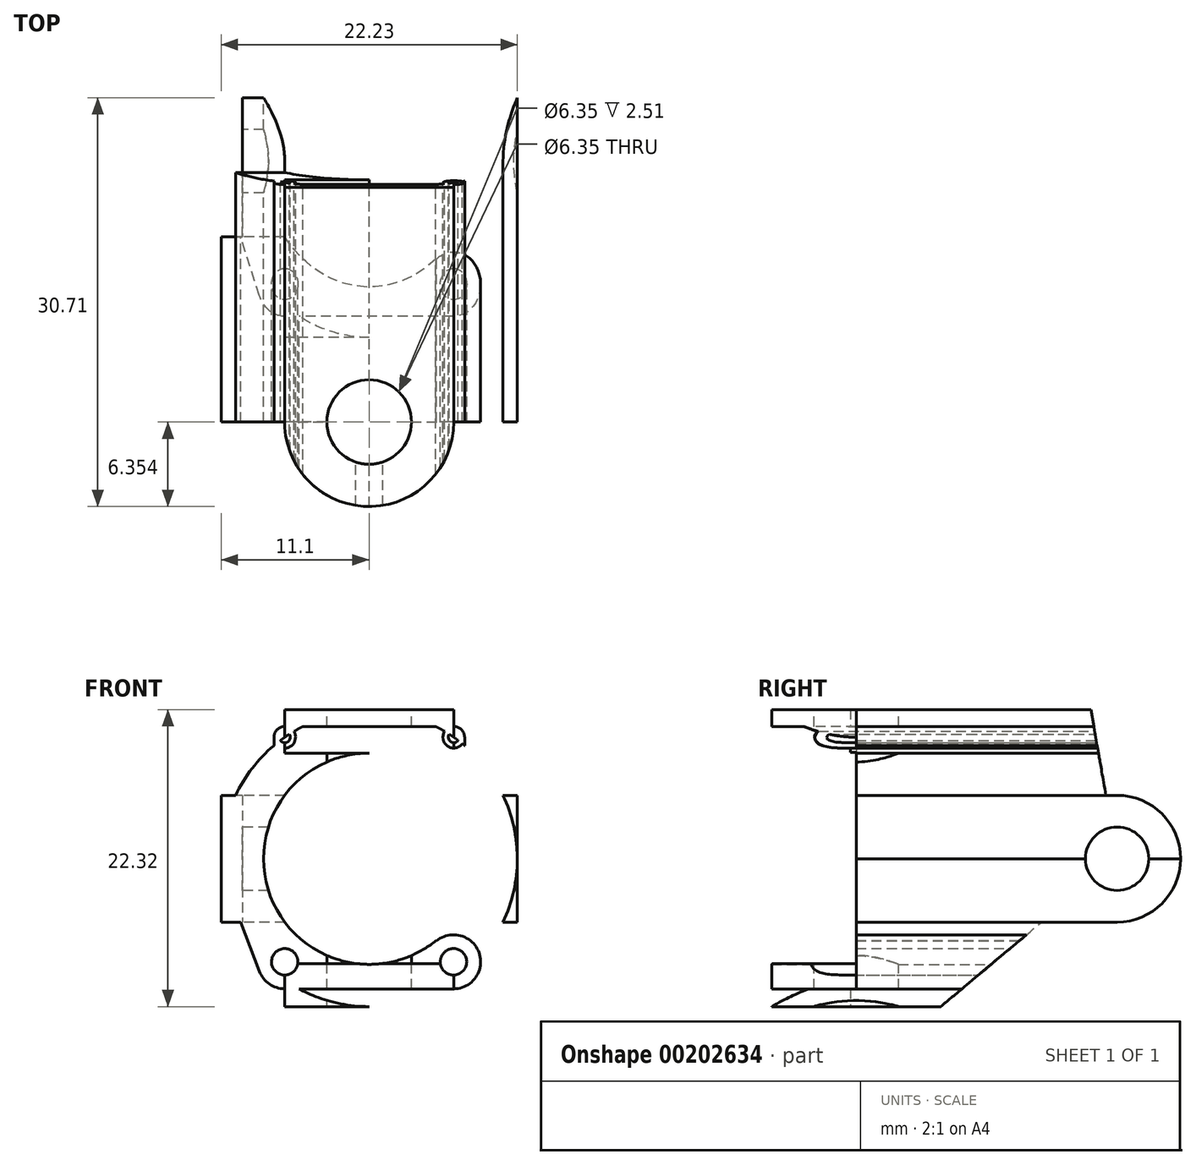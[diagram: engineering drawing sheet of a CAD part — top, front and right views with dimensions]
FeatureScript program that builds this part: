
annotation { "Feature Type Name" : "Feature", "Feature Type Description" : "" }
export const myFeature = defineFeature(function(context is Context, id is Id, definition is map)
    precondition{}
    {
        {
            var Q0;
            Q0=qCreatedBy(makeId("Front.planeOp"),FACE);
            var sketch = newSketch(context, id + "F0", { "sketchPlane" : qUnion([Q0])});
            skCircle(sketch, "E0", {"center": v(0, -0.64) * mm, "radius": 7.94 * mm});
            skCircle(sketch, "E1", {"center": v(0, -0.64) * mm, "radius": 9.53 * mm});
            skCircle(sketch, "E2", {"center": v(0, -0.64) * mm, "radius": 11.11 * mm});
            skLineSegment(sketch, "E3", {"start": v(-12.13, -0.64) * mm, "end": v(12.7, -0.64) * mm});
            skLineSegment(sketch, "E4", {"start": v(0, 12.07) * mm, "end": v(0, -13.22) * mm, "construction": true});
            skArc(sketch, "E5", {"start": v(-11.12, -0.64) * mm, "mid": v(-7.45, -7.6) * mm, "end": v(0, -10.16) * mm});
            skArc(sketch, "E6", {"start": v(0, -10.16) * mm, "mid": v(7.44, -7.6) * mm, "end": v(11.1, -0.64) * mm});
            skLineSegment(sketch, "E7", {"start": v(-9.92, -10.16) * mm, "end": v(10.05, -10.18) * mm, "construction": true});
            skLineSegment(sketch, "E8", {"start": v(-9.95, -8.38) * mm, "end": v(9.97, -8.38) * mm});
            skLineSegment(sketch, "E9", {"start": v(-6.36, -11.59) * mm, "end": v(-6.36, 12.24) * mm});
            skLineSegment(sketch, "E10", {"start": v(6.32, -11.83) * mm, "end": v(6.34, 12.33) * mm});
            skCircle(sketch, "E11", {"center": v(6.32, -8.38) * mm, "radius": 1 * mm});
            skCircle(sketch, "E12", {"center": v(6.32, -8.38) * mm, "radius": 2.03 * mm});
            skCircle(sketch, "E13", {"center": v(-6.36, -8.38) * mm, "radius": 1 * mm});
            skCircle(sketch, "E14", {"center": v(-6.36, -8.38) * mm, "radius": 2.03 * mm});
            skLineSegment(sketch, "E15", {"start": v(-10.46, -3.36) * mm, "end": v(-8.25, -9.11) * mm});
            skLineSegment(sketch, "E16", {"start": v(10.4, -3.48) * mm, "end": v(8.22, -9.12) * mm});
            skLineSegment(sketch, "E17", {"start": v(-6.36, -10.41) * mm, "end": v(6.32, -10.41) * mm});
            skCircle(sketch, "E18", {"center": v(6.34, 8.49) * mm, "radius": 0.4 * mm});
            skCircle(sketch, "E19", {"center": v(-6.36, 8.48) * mm, "radius": 0.4 * mm});
            skCircle(sketch, "E20", {"center": v(-6.36, 8.48) * mm, "radius": 0.81 * mm});
            skCircle(sketch, "E21", {"center": v(6.34, 8.49) * mm, "radius": 0.81 * mm});
            skLineSegment(sketch, "E22", {"start": v(-6.36, 9.3) * mm, "end": v(-2.52, 10.19) * mm});
            skLineSegment(sketch, "E23", {"start": v(6.34, 9.3) * mm, "end": v(2.5, 10.19) * mm});
            skLineSegment(sketch, "E24", {"start": v(5.84, 8.49) * mm, "end": v(7.39, 8.49) * mm, "construction": true});
            skLineSegment(sketch, "E25", {"start": v(-5.8, 8.48) * mm, "end": v(-7.52, 8.48) * mm, "construction": true});
            skLineSegment(sketch, "E26", {"start": v(-7.17, 8.48) * mm, "end": v(-7.17, 7.86) * mm});
            skLineSegment(sketch, "E27", {"start": v(7.15, 8.49) * mm, "end": v(7.15, 7.86) * mm});
            skLineSegment(sketch, "E28", {"start": v(7.93, -0.64) * mm, "end": v(7.93, 10.72) * mm, "construction": true});
            skLineSegment(sketch, "E29", {"start": v(-7.94, -0.64) * mm, "end": v(-7.94, 9.8) * mm, "construction": true});
            skLineSegment(sketch, "E30.bottom", {"start": v(7.93, 4.13) * mm, "end": v(11.1, 4.13) * mm});
            skLineSegment(sketch, "E30.top", {"start": v(7.93, -5.4) * mm, "end": v(11.1, -5.4) * mm});
            skLineSegment(sketch, "E30.left", {"start": v(7.93, 4.13) * mm, "end": v(7.93, -5.4) * mm});
            skLineSegment(sketch, "E30.right", {"start": v(11.1, 4.13) * mm, "end": v(11.1, -5.4) * mm});
            skLineSegment(sketch, "E31.bottom", {"start": v(-7.94, 4.13) * mm, "end": v(-11.12, 4.13) * mm});
            skLineSegment(sketch, "E31.top", {"start": v(-7.94, -5.4) * mm, "end": v(-11.12, -5.4) * mm});
            skLineSegment(sketch, "E31.left", {"start": v(-7.94, 4.13) * mm, "end": v(-7.94, -5.4) * mm});
            skLineSegment(sketch, "E31.right", {"start": v(-11.12, 4.13) * mm, "end": v(-11.12, -5.4) * mm});
            skLineSegment(sketch, "E32", {"start": v(-7.94, -5.4) * mm, "end": v(7.93, -5.4) * mm});
            skLineSegment(sketch, "E33.bottom", {"start": v(6.34, 9.3) * mm, "end": v(-6.36, 9.3) * mm});
            skLineSegment(sketch, "E33.top", {"start": v(6.34, 10.57) * mm, "end": v(-6.36, 10.57) * mm});
            skLineSegment(sketch, "E33.left", {"start": v(6.34, 9.3) * mm, "end": v(6.34, 10.57) * mm});
            skLineSegment(sketch, "E33.right", {"start": v(-6.36, 9.3) * mm, "end": v(-6.36, 10.57) * mm});
            skLineSegment(sketch, "E34", {"start": v(0, 7.3) * mm, "end": v(11, 7.3) * mm});
            skLineSegment(sketch, "E35", {"start": v(11, 7.3) * mm, "end": v(-10.84, 7.3) * mm});
            skLineSegment(sketch, "E36.bottom", {"start": v(6.32, -10.41) * mm, "end": v(0, -10.41) * mm});
            skLineSegment(sketch, "E36.top", {"start": v(6.32, -11.75) * mm, "end": v(0, -11.75) * mm});
            skLineSegment(sketch, "E36.left", {"start": v(6.32, -10.41) * mm, "end": v(6.32, -11.75) * mm});
            skLineSegment(sketch, "E36.right", {"start": v(0, -10.41) * mm, "end": v(0, -11.75) * mm});
            skLineSegment(sketch, "E37.bottom", {"start": v(-6.36, -10.41) * mm, "end": v(0, -10.41) * mm});
            skLineSegment(sketch, "E37.top", {"start": v(-6.36, -11.75) * mm, "end": v(0, -11.75) * mm});
            skLineSegment(sketch, "E37.left", {"start": v(-6.36, -10.41) * mm, "end": v(-6.36, -11.75) * mm});
            skLineSegment(sketch, "E38", {"start": v(6.32, -8.38) * mm, "end": v(0, -0.64) * mm});
            skSolve(sketch);
        }
        {
            var Q0;
            {var subQ0=sQuery(id+"F0.wireOp",EDGE,"E35");var subQ15=sQuery(id+"F0.wireOp",EDGE,"E1");var subQ16=makeQuery(id+"F0.imprint","INTERSECT",VERTEX,{"disambiguationData":[OD(0.0)],"derivedFrom":[subQ15,subQ0]});Q0=makeQuery(id+"F0.imprint","IMPRINT",FACE,{"disambiguationData":[TD([[makeQuery(id+"F0.imprint","IMPRINT",EDGE,{"disambiguationData":[TD([[subQ16,-1.0]])],"derivedFrom":subQ15}),-1.0]])]});}
            var Q1;
            {var subQ0=sQuery(id+"F0.wireOp",EDGE,"E35");var subQ1=sQuery(id+"F0.wireOp",EDGE,"E1");var subQ2=makeQuery(id+"F0.imprint","INTERSECT",VERTEX,{"disambiguationData":[OD(0.0)],"derivedFrom":[subQ1,subQ0]});Q1=makeQuery(id+"F0.imprint","IMPRINT",FACE,{"disambiguationData":[TD([[makeQuery(id+"F0.imprint","IMPRINT",EDGE,{"disambiguationData":[TD([[subQ2,-1.0]])],"derivedFrom":subQ1}),1.0]])]});}
            var Q2;
            {var subQ0=sQuery(id+"F0.wireOp",EDGE,"E18");var subQ1=sQuery(id+"F0.wireOp",EDGE,"E2");var subQ2=makeQuery(id+"F0.imprint","INTERSECT",VERTEX,{"disambiguationData":[OD(1.0)],"derivedFrom":[subQ1,subQ0]});Q2=makeQuery(id+"F0.imprint","IMPRINT",FACE,{"disambiguationData":[TD([[makeQuery(id+"F0.imprint","IMPRINT",EDGE,{"disambiguationData":[TD([[subQ2,-1.0]])],"derivedFrom":subQ1}),1.0]])]});}
            var Q3;
            {var subQ0=sQuery(id+"F0.wireOp",EDGE,"E21");var subQ1=sQuery(id+"F0.wireOp",EDGE,"E2");var subQ2=makeQuery(id+"F0.imprint","INTERSECT",VERTEX,{"disambiguationData":[OD(0.0)],"derivedFrom":[subQ1,subQ0]});Q3=makeQuery(id+"F0.imprint","IMPRINT",FACE,{"disambiguationData":[TD([[makeQuery(id+"F0.imprint","IMPRINT",EDGE,{"disambiguationData":[TD([[subQ2,-1.0]])],"derivedFrom":subQ1}),1.0]])]});}
            var Q4;
            {var subQ1=sQuery(id+"F0.wireOp",EDGE,"E2");var subQ5=sQuery(id+"F0.wireOp",EDGE,"E21");var subQ8=makeQuery(id+"F0.imprint","INTERSECT",VERTEX,{"disambiguationData":[OD(0.0)],"derivedFrom":[subQ1,subQ5]});Q4=makeQuery(id+"F0.imprint","IMPRINT",FACE,{"disambiguationData":[TD([[makeQuery(id+"F0.imprint","IMPRINT",EDGE,{"disambiguationData":[TD([[subQ8,-1.0]])],"derivedFrom":subQ1}),-1.0]])]});}
            var Q5;
            {var subQ0=sQuery(id+"F0.wireOp",EDGE,"E18");var subQ1=sQuery(id+"F0.wireOp",EDGE,"E2");var subQ2=makeQuery(id+"F0.imprint","INTERSECT",VERTEX,{"disambiguationData":[OD(1.0)],"derivedFrom":[subQ1,subQ0]});Q5=makeQuery(id+"F0.imprint","IMPRINT",FACE,{"disambiguationData":[TD([[makeQuery(id+"F0.imprint","IMPRINT",EDGE,{"disambiguationData":[TD([[subQ2,-1.0]])],"derivedFrom":subQ1}),-1.0]])]});}
            var Q6;
            {var subQ0=sQuery(id+"F0.wireOp",EDGE,"E21");var subQ1=sQuery(id+"F0.wireOp",EDGE,"E2");var subQ2=makeQuery(id+"F0.imprint","INTERSECT",VERTEX,{"disambiguationData":[OD(1.0)],"derivedFrom":[subQ1,subQ0]});Q6=makeQuery(id+"F0.imprint","IMPRINT",FACE,{"disambiguationData":[TD([[makeQuery(id+"F0.imprint","IMPRINT",EDGE,{"disambiguationData":[TD([[subQ2,-1.0]])],"derivedFrom":subQ1}),-1.0]])]});}
            var Q7;
            {var subQ0=sQuery(id+"F0.wireOp",EDGE,"E23");Q7=makeQuery(id+"F0.imprint","IMPRINT",FACE,{"disambiguationData":[TD([[makeQuery(id+"F0.imprint","IMPRINT",EDGE,{"derivedFrom":subQ0}),1.0]])]});}
            var Q8;
            {var subQ0=sQuery(id+"F0.wireOp",EDGE,"E23");Q8=makeQuery(id+"F0.imprint","IMPRINT",FACE,{"disambiguationData":[TD([[makeQuery(id+"F0.imprint","IMPRINT",EDGE,{"derivedFrom":subQ0}),-1.0]])]});}
            var Q9;
            {var subQ0=sQuery(id+"F0.wireOp",EDGE,"E2");var subQ1=makeQuery(id+"F0.imprint","INTERSECT",VERTEX,{"derivedFrom":[subQ0,sQuery(id+"F0.wireOp",EDGE,"E23")]});Q9=makeQuery(id+"F0.imprint","IMPRINT",FACE,{"disambiguationData":[TD([[makeQuery(id+"F0.imprint","IMPRINT",EDGE,{"disambiguationData":[TD([[subQ1,1.0]])],"derivedFrom":subQ0}),1.0]])]});}
            var Q10;
            {var subQ0=sQuery(id+"F0.wireOp",EDGE,"E22");var subQ1=sQuery(id+"F0.wireOp",EDGE,"E2");var subQ2=makeQuery(id+"F0.imprint","INTERSECT",VERTEX,{"derivedFrom":[subQ1,subQ0]});Q10=makeQuery(id+"F0.imprint","IMPRINT",FACE,{"disambiguationData":[TD([[makeQuery(id+"F0.imprint","IMPRINT",EDGE,{"disambiguationData":[TD([[subQ2,-1.0]])],"derivedFrom":subQ1}),-1.0]])]});}
            var Q11;
            {var subQ0=sQuery(id+"F0.wireOp",EDGE,"E33.bottom");var subQ1=sQuery(id+"F0.wireOp",EDGE,"E2");var subQ2=makeQuery(id+"F0.imprint","INTERSECT",VERTEX,{"disambiguationData":[OD(1.0)],"derivedFrom":[subQ1,subQ0]});Q11=makeQuery(id+"F0.imprint","IMPRINT",FACE,{"disambiguationData":[TD([[makeQuery(id+"F0.imprint","IMPRINT",EDGE,{"disambiguationData":[TD([[subQ2,-1.0]])],"derivedFrom":subQ1}),-1.0]])]});}
            var Q12;
            {var subQ0=sQuery(id+"F0.wireOp",EDGE,"E20");var subQ1=sQuery(id+"F0.wireOp",EDGE,"E2");var subQ2=makeQuery(id+"F0.imprint","INTERSECT",VERTEX,{"disambiguationData":[OD(0.0)],"derivedFrom":[subQ1,subQ0]});Q12=makeQuery(id+"F0.imprint","IMPRINT",FACE,{"disambiguationData":[TD([[makeQuery(id+"F0.imprint","IMPRINT",EDGE,{"disambiguationData":[TD([[subQ2,-1.0]])],"derivedFrom":subQ1}),-1.0]])]});}
            var Q13;
            {var subQ4=sQuery(id+"F0.wireOp",EDGE,"E19");var subQ5=sQuery(id+"F0.wireOp",EDGE,"E2");var subQ6=makeQuery(id+"F0.imprint","INTERSECT",VERTEX,{"disambiguationData":[OD(1.0)],"derivedFrom":[subQ5,subQ4]});Q13=makeQuery(id+"F0.imprint","IMPRINT",FACE,{"disambiguationData":[TD([[makeQuery(id+"F0.imprint","IMPRINT",EDGE,{"disambiguationData":[TD([[subQ6,-1.0]])],"derivedFrom":subQ5}),-1.0]])]});}
            var Q14;
            {var subQ0=sQuery(id+"F0.wireOp",EDGE,"E19");var subQ1=sQuery(id+"F0.wireOp",EDGE,"E2");var subQ2=makeQuery(id+"F0.imprint","INTERSECT",VERTEX,{"disambiguationData":[OD(1.0)],"derivedFrom":[subQ1,subQ0]});Q14=makeQuery(id+"F0.imprint","IMPRINT",FACE,{"disambiguationData":[TD([[makeQuery(id+"F0.imprint","IMPRINT",EDGE,{"disambiguationData":[TD([[subQ2,-1.0]])],"derivedFrom":subQ1}),1.0]])]});}
            var Q15;
            {var subQ0=sQuery(id+"F0.wireOp",EDGE,"E20");var subQ1=sQuery(id+"F0.wireOp",EDGE,"E2");var subQ2=makeQuery(id+"F0.imprint","INTERSECT",VERTEX,{"disambiguationData":[OD(0.0)],"derivedFrom":[subQ1,subQ0]});Q15=makeQuery(id+"F0.imprint","IMPRINT",FACE,{"disambiguationData":[TD([[makeQuery(id+"F0.imprint","IMPRINT",EDGE,{"disambiguationData":[TD([[subQ2,-1.0]])],"derivedFrom":subQ1}),1.0]])]});}
            var Q16;
            {var subQ0=sQuery(id+"F0.wireOp",EDGE,"E26");Q16=makeQuery(id+"F0.imprint","IMPRINT",FACE,{"disambiguationData":[TD([[makeQuery(id+"F0.imprint","IMPRINT",EDGE,{"derivedFrom":subQ0}),1.0]])]});}
            var Q17;
            {var subQ1=sQuery(id+"F0.wireOp",EDGE,"E2");var subQ7=makeQuery(id+"F0.imprint","INTERSECT",VERTEX,{"derivedFrom":[subQ1,sQuery(id+"F0.wireOp",EDGE,"E26")]});Q17=makeQuery(id+"F0.imprint","IMPRINT",FACE,{"disambiguationData":[TD([[makeQuery(id+"F0.imprint","IMPRINT",EDGE,{"disambiguationData":[TD([[subQ7,1.0]])],"derivedFrom":subQ1}),1.0]])]});}
            var Q18;
            {var subQ0=sQuery(id+"F0.wireOp",EDGE,"E35");var subQ1=sQuery(id+"F0.wireOp",EDGE,"E0");var subQ2=makeQuery(id+"F0.imprint","INTERSECT",VERTEX,{"derivedFrom":[subQ1,subQ0]});Q18=makeQuery(id+"F0.imprint","IMPRINT",FACE,{"disambiguationData":[TD([[makeQuery(id+"F0.imprint","IMPRINT",EDGE,{"disambiguationData":[TD([[subQ2,-1.0]])],"derivedFrom":subQ1}),-1.0]])]});}
            var Q19;
            {var subQ0=sQuery(id+"F0.wireOp",EDGE,"E35");var subQ1=sQuery(id+"F0.wireOp",EDGE,"E1");var subQ2=makeQuery(id+"F0.imprint","INTERSECT",VERTEX,{"disambiguationData":[OD(1.0)],"derivedFrom":[subQ1,subQ0]});Q19=makeQuery(id+"F0.imprint","IMPRINT",FACE,{"disambiguationData":[TD([[makeQuery(id+"F0.imprint","IMPRINT",EDGE,{"disambiguationData":[TD([[subQ2,-1.0]])],"derivedFrom":subQ1}),-1.0]])]});}
            var Q20;
            {var subQ3=sQuery(id+"F0.wireOp",EDGE,"E1");var subQ5=sQuery(id+"F0.wireOp",EDGE,"E9");var subQ6=makeQuery(id+"F0.imprint","INTERSECT",VERTEX,{"disambiguationData":[OD(0.0)],"derivedFrom":[subQ3,subQ5]});Q20=makeQuery(id+"F0.imprint","IMPRINT",FACE,{"disambiguationData":[TD([[makeQuery(id+"F0.imprint","IMPRINT",EDGE,{"disambiguationData":[TD([[subQ6,-1.0]])],"derivedFrom":subQ3}),-1.0]])]});}
            var Q21;
            {var subQ3=sQuery(id+"F0.wireOp",EDGE,"E1");var subQ5=sQuery(id+"F0.wireOp",EDGE,"E9");var subQ6=makeQuery(id+"F0.imprint","INTERSECT",VERTEX,{"disambiguationData":[OD(0.0)],"derivedFrom":[subQ3,subQ5]});Q21=makeQuery(id+"F0.imprint","IMPRINT",FACE,{"disambiguationData":[TD([[makeQuery(id+"F0.imprint","IMPRINT",EDGE,{"disambiguationData":[TD([[subQ6,-1.0]])],"derivedFrom":subQ3}),1.0]])]});}
            var Q22;
            {var subQ0=sQuery(id+"F0.wireOp",EDGE,"E31.bottom");var subQ1=sQuery(id+"F0.wireOp",EDGE,"E1");var subQ2=makeQuery(id+"F0.imprint","INTERSECT",VERTEX,{"derivedFrom":[subQ1,subQ0]});Q22=makeQuery(id+"F0.imprint","IMPRINT",FACE,{"disambiguationData":[TD([[makeQuery(id+"F0.imprint","IMPRINT",EDGE,{"disambiguationData":[TD([[subQ2,-1.0]])],"derivedFrom":subQ1}),1.0]])]});}
            var Q23;
            {var subQ0=sQuery(id+"F0.wireOp",EDGE,"E31.bottom");var subQ1=sQuery(id+"F0.wireOp",EDGE,"E1");var subQ2=makeQuery(id+"F0.imprint","INTERSECT",VERTEX,{"derivedFrom":[subQ1,subQ0]});Q23=makeQuery(id+"F0.imprint","IMPRINT",FACE,{"disambiguationData":[TD([[makeQuery(id+"F0.imprint","IMPRINT",EDGE,{"disambiguationData":[TD([[subQ2,-1.0]])],"derivedFrom":subQ1}),-1.0]])]});}
            var Q24;
            {var subQ0=sQuery(id+"F0.wireOp",EDGE,"E31.right");var subQ3=sQuery(id+"F0.wireOp",EDGE,"E31.bottom");var subQ5=makeQuery(id+"F0.imprint","INTERSECT",VERTEX,{"derivedFrom":[subQ3,subQ0]});Q24=makeQuery(id+"F0.imprint","IMPRINT",FACE,{"disambiguationData":[TD([[makeQuery(id+"F0.imprint","IMPRINT",EDGE,{"disambiguationData":[TD([[subQ5,1.0]])],"derivedFrom":subQ3}),1.0]])]});}
            var Q25;
            {var subQ0=sQuery(id+"F0.wireOp",EDGE,"E3");var subQ1=sQuery(id+"F0.wireOp",EDGE,"E1");var subQ2=makeQuery(id+"F0.imprint","INTERSECT",VERTEX,{"disambiguationData":[OD(1.0)],"derivedFrom":[subQ1,subQ0]});Q25=makeQuery(id+"F0.imprint","IMPRINT",FACE,{"disambiguationData":[TD([[makeQuery(id+"F0.imprint","IMPRINT",EDGE,{"disambiguationData":[TD([[subQ2,-1.0]])],"derivedFrom":subQ1}),1.0]])]});}
            var Q26;
            {var subQ0=sQuery(id+"F0.wireOp",EDGE,"E31.left");var subQ1=sQuery(id+"F0.wireOp",EDGE,"E0");var subQ2=makeQuery(id+"F0.imprint","INTERSECT",VERTEX,{"derivedFrom":[subQ1,sQuery(id+"F0.wireOp",EDGE,"E3"),subQ0]});Q26=makeQuery(id+"F0.imprint","IMPRINT",FACE,{"disambiguationData":[TD([[makeQuery(id+"F0.imprint","IMPRINT",EDGE,{"disambiguationData":[TD([[subQ2,-1.0]])],"derivedFrom":subQ1}),-1.0]])]});}
            var Q27;
            {var subQ1=sQuery(id+"F0.wireOp",EDGE,"E1");var subQ7=sQuery(id+"F0.wireOp",EDGE,"E31.top");var subQ9=makeQuery(id+"F0.imprint","INTERSECT",VERTEX,{"derivedFrom":[subQ1,subQ7]});Q27=makeQuery(id+"F0.imprint","IMPRINT",FACE,{"disambiguationData":[TD([[makeQuery(id+"F0.imprint","IMPRINT",EDGE,{"disambiguationData":[TD([[subQ9,-1.0]])],"derivedFrom":subQ1}),1.0]])]});}
            var Q28;
            {var subQ0=sQuery(id+"F0.wireOp",EDGE,"E8");var subQ1=sQuery(id+"F0.wireOp",EDGE,"E0");var subQ2=makeQuery(id+"F0.imprint","INTERSECT",VERTEX,{"disambiguationData":[OD(0.0)],"derivedFrom":[subQ1,subQ0]});Q28=makeQuery(id+"F0.imprint","IMPRINT",FACE,{"disambiguationData":[TD([[makeQuery(id+"F0.imprint","IMPRINT",EDGE,{"disambiguationData":[TD([[subQ2,1.0]])],"derivedFrom":subQ0}),1.0]])]});}
            var Q29;
            {var subQ0=sQuery(id+"F0.wireOp",EDGE,"E8");var subQ1=sQuery(id+"F0.wireOp",EDGE,"E0");var subQ2=makeQuery(id+"F0.imprint","INTERSECT",VERTEX,{"disambiguationData":[OD(0.0)],"derivedFrom":[subQ1,subQ0]});Q29=makeQuery(id+"F0.imprint","IMPRINT",FACE,{"disambiguationData":[TD([[makeQuery(id+"F0.imprint","IMPRINT",EDGE,{"disambiguationData":[TD([[subQ2,-1.0]])],"derivedFrom":subQ1}),-1.0]])]});}
            var Q30;
            {var subQ0=sQuery(id+"F0.wireOp",EDGE,"E8");var subQ1=sQuery(id+"F0.wireOp",EDGE,"E0");var subQ2=makeQuery(id+"F0.imprint","INTERSECT",VERTEX,{"disambiguationData":[OD(1.0)],"derivedFrom":[subQ1,subQ0]});Q30=makeQuery(id+"F0.imprint","IMPRINT",FACE,{"disambiguationData":[TD([[makeQuery(id+"F0.imprint","IMPRINT",EDGE,{"disambiguationData":[TD([[subQ2,-1.0]])],"derivedFrom":subQ1}),-1.0]])]});}
            var Q31;
            {var subQ0=sQuery(id+"F0.wireOp",EDGE,"E12");var subQ1=sQuery(id+"F0.wireOp",EDGE,"E8");var subQ2=makeQuery(id+"F0.imprint","INTERSECT",VERTEX,{"disambiguationData":[OD(0.0)],"derivedFrom":[subQ1,subQ0]});Q31=makeQuery(id+"F0.imprint","IMPRINT",FACE,{"disambiguationData":[TD([[makeQuery(id+"F0.imprint","IMPRINT",EDGE,{"disambiguationData":[TD([[subQ2,-1.0]])],"derivedFrom":subQ1}),1.0]])]});}
            var Q32;
            {var subQ0=sQuery(id+"F0.wireOp",EDGE,"E11");var subQ1=sQuery(id+"F0.wireOp",EDGE,"E10");var subQ2=makeQuery(id+"F0.imprint","INTERSECT",VERTEX,{"disambiguationData":[OD(1.0)],"derivedFrom":[subQ1,subQ0]});Q32=makeQuery(id+"F0.imprint","IMPRINT",FACE,{"disambiguationData":[TD([[makeQuery(id+"F0.imprint","IMPRINT",EDGE,{"disambiguationData":[TD([[subQ2,-1.0]])],"derivedFrom":subQ1}),1.0]])]});}
            var Q33;
            {var subQ0=sQuery(id+"F0.wireOp",EDGE,"E11");var subQ1=sQuery(id+"F0.wireOp",EDGE,"E1");var subQ2=makeQuery(id+"F0.imprint","INTERSECT",VERTEX,{"disambiguationData":[OD(1.0)],"derivedFrom":[subQ1,subQ0]});Q33=makeQuery(id+"F0.imprint","IMPRINT",FACE,{"disambiguationData":[TD([[makeQuery(id+"F0.imprint","IMPRINT",EDGE,{"disambiguationData":[TD([[subQ2,-1.0]])],"derivedFrom":subQ1}),1.0]])]});}
            var Q34;
            {var subQ0=sQuery(id+"F0.wireOp",EDGE,"E11");var subQ1=sQuery(id+"F0.wireOp",EDGE,"E1");var subQ2=makeQuery(id+"F0.imprint","INTERSECT",VERTEX,{"disambiguationData":[OD(1.0)],"derivedFrom":[subQ1,subQ0]});Q34=makeQuery(id+"F0.imprint","IMPRINT",FACE,{"disambiguationData":[TD([[makeQuery(id+"F0.imprint","IMPRINT",EDGE,{"disambiguationData":[TD([[subQ2,-1.0]])],"derivedFrom":subQ1}),-1.0]])]});}
            var Q35;
            {var subQ3=sQuery(id+"F0.wireOp",EDGE,"E8");var subQ5=sQuery(id+"F0.wireOp",EDGE,"E2");var subQ6=makeQuery(id+"F0.imprint","INTERSECT",VERTEX,{"disambiguationData":[OD(1.0)],"derivedFrom":[subQ5,subQ3]});Q35=makeQuery(id+"F0.imprint","IMPRINT",FACE,{"disambiguationData":[TD([[makeQuery(id+"F0.imprint","IMPRINT",EDGE,{"disambiguationData":[TD([[subQ6,-1.0]])],"derivedFrom":subQ5}),1.0]])]});}
            var Q36;
            {var subQ0=sQuery(id+"F0.wireOp",EDGE,"E8");var subQ1=sQuery(id+"F0.wireOp",EDGE,"E2");var subQ2=makeQuery(id+"F0.imprint","INTERSECT",VERTEX,{"disambiguationData":[OD(1.0)],"derivedFrom":[subQ1,subQ0]});Q36=makeQuery(id+"F0.imprint","IMPRINT",FACE,{"disambiguationData":[TD([[makeQuery(id+"F0.imprint","IMPRINT",EDGE,{"disambiguationData":[TD([[subQ2,-1.0]])],"derivedFrom":subQ1}),-1.0]])]});}
            var Q37;
            {var subQ2=sQuery(id+"F0.wireOp",EDGE,"E10");var subQ6=sQuery(id+"F0.wireOp",EDGE,"E2");var subQ7=makeQuery(id+"F0.imprint","INTERSECT",VERTEX,{"disambiguationData":[OD(1.0)],"derivedFrom":[subQ6,subQ2]});Q37=makeQuery(id+"F0.imprint","IMPRINT",FACE,{"disambiguationData":[TD([[makeQuery(id+"F0.imprint","IMPRINT",EDGE,{"disambiguationData":[TD([[subQ7,-1.0]])],"derivedFrom":subQ6}),-1.0]])]});}
            var Q38;
            {var subQ0=sQuery(id+"F0.wireOp",EDGE,"E10");var subQ1=sQuery(id+"F0.wireOp",EDGE,"E2");var subQ2=makeQuery(id+"F0.imprint","INTERSECT",VERTEX,{"disambiguationData":[OD(1.0)],"derivedFrom":[subQ1,subQ0]});Q38=makeQuery(id+"F0.imprint","IMPRINT",FACE,{"disambiguationData":[TD([[makeQuery(id+"F0.imprint","IMPRINT",EDGE,{"disambiguationData":[TD([[subQ2,-1.0]])],"derivedFrom":subQ1}),1.0]])]});}
            var Q39;
            {var subQ5=sQuery(id+"F0.wireOp",EDGE,"E2");var subQ7=sQuery(id+"F0.wireOp",EDGE,"E12");var subQ9=makeQuery(id+"F0.imprint","INTERSECT",VERTEX,{"disambiguationData":[OD(0.0)],"derivedFrom":[subQ5,subQ7]});Q39=makeQuery(id+"F0.imprint","IMPRINT",FACE,{"disambiguationData":[TD([[makeQuery(id+"F0.imprint","IMPRINT",EDGE,{"disambiguationData":[TD([[subQ9,-1.0]])],"derivedFrom":subQ5}),1.0]])]});}
            var Q40;
            {var subQ0=sQuery(id+"F0.wireOp",EDGE,"E12");var subQ1=sQuery(id+"F0.wireOp",EDGE,"E1");var subQ2=makeQuery(id+"F0.imprint","INTERSECT",VERTEX,{"disambiguationData":[OD(0.0)],"derivedFrom":[subQ1,subQ0]});Q40=makeQuery(id+"F0.imprint","IMPRINT",FACE,{"disambiguationData":[TD([[makeQuery(id+"F0.imprint","IMPRINT",EDGE,{"disambiguationData":[TD([[subQ2,-1.0]])],"derivedFrom":subQ1}),1.0]])]});}
            var Q41;
            {var subQ0=sQuery(id+"F0.wireOp",EDGE,"E12");var subQ1=sQuery(id+"F0.wireOp",EDGE,"E1");var subQ2=makeQuery(id+"F0.imprint","INTERSECT",VERTEX,{"disambiguationData":[OD(0.0)],"derivedFrom":[subQ1,subQ0]});Q41=makeQuery(id+"F0.imprint","IMPRINT",FACE,{"disambiguationData":[TD([[makeQuery(id+"F0.imprint","IMPRINT",EDGE,{"disambiguationData":[TD([[subQ2,-1.0]])],"derivedFrom":subQ1}),-1.0]])]});}
            var Q42;
            {var subQ0=sQuery(id+"F0.wireOp",EDGE,"E12");var subQ1=sQuery(id+"F0.wireOp",EDGE,"E2");var subQ2=makeQuery(id+"F0.imprint","INTERSECT",VERTEX,{"disambiguationData":[OD(0.0)],"derivedFrom":[subQ1,subQ0]});Q42=makeQuery(id+"F0.imprint","IMPRINT",FACE,{"disambiguationData":[TD([[makeQuery(id+"F0.imprint","IMPRINT",EDGE,{"disambiguationData":[TD([[subQ2,-1.0]])],"derivedFrom":subQ1}),-1.0]])]});}
            var Q43;
            {var subQ5=sQuery(id+"F0.wireOp",EDGE,"E14");var subQ8=sQuery(id+"F0.wireOp",EDGE,"E2");var subQ11=makeQuery(id+"F0.imprint","INTERSECT",VERTEX,{"disambiguationData":[OD(1.0)],"derivedFrom":[subQ8,subQ5]});Q43=makeQuery(id+"F0.imprint","IMPRINT",FACE,{"disambiguationData":[TD([[makeQuery(id+"F0.imprint","IMPRINT",EDGE,{"disambiguationData":[TD([[subQ11,-1.0]])],"derivedFrom":subQ8}),1.0]])]});}
            var Q44;
            {var subQ1=sQuery(id+"F0.wireOp",EDGE,"E1");var subQ3=sQuery(id+"F0.wireOp",EDGE,"E12");var subQ4=makeQuery(id+"F0.imprint","INTERSECT",VERTEX,{"disambiguationData":[OD(0.0)],"derivedFrom":[subQ1,subQ3]});Q44=makeQuery(id+"F0.imprint","IMPRINT",FACE,{"disambiguationData":[TD([[makeQuery(id+"F0.imprint","IMPRINT",EDGE,{"disambiguationData":[TD([[subQ4,-1.0]])],"derivedFrom":subQ3}),-1.0]])]});}
            var Q45;
            {var subQ0=sQuery(id+"F0.wireOp",EDGE,"E36.bottom");var subQ1=sQuery(id+"F0.wireOp",EDGE,"E2");var subQ2=makeQuery(id+"F0.imprint","INTERSECT",VERTEX,{"derivedFrom":[subQ1,subQ0]});Q45=makeQuery(id+"F0.imprint","IMPRINT",FACE,{"disambiguationData":[TD([[makeQuery(id+"F0.imprint","IMPRINT",EDGE,{"disambiguationData":[TD([[subQ2,-1.0]])],"derivedFrom":subQ1}),-1.0]])]});}
            var Q46;
            {var subQ1=sQuery(id+"F0.wireOp",EDGE,"E2");var subQ3=sQuery(id+"F0.wireOp",EDGE,"E36.bottom");var subQ4=makeQuery(id+"F0.imprint","INTERSECT",VERTEX,{"derivedFrom":[subQ1,subQ3]});Q46=makeQuery(id+"F0.imprint","IMPRINT",FACE,{"disambiguationData":[TD([[makeQuery(id+"F0.imprint","IMPRINT",EDGE,{"disambiguationData":[TD([[subQ4,1.0]])],"derivedFrom":subQ1}),-1.0]])]});}
            var Q47;
            {var subQ0=sQuery(id+"F0.wireOp",EDGE,"E36.right");Q47=makeQuery(id+"F0.imprint","IMPRINT",FACE,{"disambiguationData":[TD([[makeQuery(id+"F0.imprint","IMPRINT",EDGE,{"derivedFrom":subQ0}),1.0]])]});}
            var Q48;
            {var subQ0=sQuery(id+"F0.wireOp",EDGE,"E36.right");Q48=makeQuery(id+"F0.imprint","IMPRINT",FACE,{"disambiguationData":[TD([[makeQuery(id+"F0.imprint","IMPRINT",EDGE,{"derivedFrom":subQ0}),-1.0]])]});}
            var Q49;
            {var subQ0=sQuery(id+"F0.wireOp",EDGE,"E37.top");Q49=makeQuery(id+"F0.imprint","IMPRINT",FACE,{"disambiguationData":[TD([[makeQuery(id+"F0.imprint","IMPRINT",EDGE,{"derivedFrom":subQ0}),1.0]])]});}
            var Q50;
            {var subQ1=sQuery(id+"F0.wireOp",EDGE,"E1");var subQ3=sQuery(id+"F0.wireOp",EDGE,"E14");var subQ4=makeQuery(id+"F0.imprint","INTERSECT",VERTEX,{"disambiguationData":[OD(1.0)],"derivedFrom":[subQ1,subQ3]});Q50=makeQuery(id+"F0.imprint","IMPRINT",FACE,{"disambiguationData":[TD([[makeQuery(id+"F0.imprint","IMPRINT",EDGE,{"disambiguationData":[TD([[subQ4,1.0]])],"derivedFrom":subQ3}),-1.0]])]});}
            var Q51;
            {var subQ0=sQuery(id+"F0.wireOp",EDGE,"E14");var subQ1=sQuery(id+"F0.wireOp",EDGE,"E2");var subQ2=makeQuery(id+"F0.imprint","INTERSECT",VERTEX,{"disambiguationData":[OD(1.0)],"derivedFrom":[subQ1,subQ0]});Q51=makeQuery(id+"F0.imprint","IMPRINT",FACE,{"disambiguationData":[TD([[makeQuery(id+"F0.imprint","IMPRINT",EDGE,{"disambiguationData":[TD([[subQ2,-1.0]])],"derivedFrom":subQ1}),-1.0]])]});}
            var Q52;
            {var subQ0=sQuery(id+"F0.wireOp",EDGE,"E13");var subQ1=sQuery(id+"F0.wireOp",EDGE,"E8");var subQ2=makeQuery(id+"F0.imprint","INTERSECT",VERTEX,{"disambiguationData":[OD(1.0)],"derivedFrom":[subQ1,subQ0]});Q52=makeQuery(id+"F0.imprint","IMPRINT",FACE,{"disambiguationData":[TD([[makeQuery(id+"F0.imprint","IMPRINT",EDGE,{"disambiguationData":[TD([[subQ2,-1.0]])],"derivedFrom":subQ1}),1.0]])]});}
            var Q53;
            {var subQ0=sQuery(id+"F0.wireOp",EDGE,"E14");var subQ1=sQuery(id+"F0.wireOp",EDGE,"E1");var subQ2=makeQuery(id+"F0.imprint","INTERSECT",VERTEX,{"disambiguationData":[OD(0.0)],"derivedFrom":[subQ1,subQ0]});Q53=makeQuery(id+"F0.imprint","IMPRINT",FACE,{"disambiguationData":[TD([[makeQuery(id+"F0.imprint","IMPRINT",EDGE,{"disambiguationData":[TD([[subQ2,-1.0]])],"derivedFrom":subQ1}),1.0]])]});}
            var Q54;
            {var subQ0=sQuery(id+"F0.wireOp",EDGE,"E14");var subQ1=sQuery(id+"F0.wireOp",EDGE,"E1");var subQ2=makeQuery(id+"F0.imprint","INTERSECT",VERTEX,{"disambiguationData":[OD(0.0)],"derivedFrom":[subQ1,subQ0]});Q54=makeQuery(id+"F0.imprint","IMPRINT",FACE,{"disambiguationData":[TD([[makeQuery(id+"F0.imprint","IMPRINT",EDGE,{"disambiguationData":[TD([[subQ2,-1.0]])],"derivedFrom":subQ1}),-1.0]])]});}
            var Q55;
            {var subQ5=sQuery(id+"F0.wireOp",EDGE,"E2");var subQ7=sQuery(id+"F0.wireOp",EDGE,"E14");var subQ9=makeQuery(id+"F0.imprint","INTERSECT",VERTEX,{"disambiguationData":[OD(0.0)],"derivedFrom":[subQ5,subQ7]});Q55=makeQuery(id+"F0.imprint","IMPRINT",FACE,{"disambiguationData":[TD([[makeQuery(id+"F0.imprint","IMPRINT",EDGE,{"disambiguationData":[TD([[subQ9,-1.0]])],"derivedFrom":subQ5}),1.0]])]});}
            var Q56;
            {var subQ0=sQuery(id+"F0.wireOp",EDGE,"E8");var subQ1=sQuery(id+"F0.wireOp",EDGE,"E2");var subQ2=makeQuery(id+"F0.imprint","INTERSECT",VERTEX,{"disambiguationData":[OD(0.0)],"derivedFrom":[subQ1,subQ0]});Q56=makeQuery(id+"F0.imprint","IMPRINT",FACE,{"disambiguationData":[TD([[makeQuery(id+"F0.imprint","IMPRINT",EDGE,{"disambiguationData":[TD([[subQ2,-1.0]])],"derivedFrom":subQ1}),1.0]])]});}
            var Q57;
            {var subQ2=sQuery(id+"F0.wireOp",EDGE,"E8");var subQ6=sQuery(id+"F0.wireOp",EDGE,"E2");var subQ8=makeQuery(id+"F0.imprint","INTERSECT",VERTEX,{"disambiguationData":[OD(0.0)],"derivedFrom":[subQ6,subQ2]});Q57=makeQuery(id+"F0.imprint","IMPRINT",FACE,{"disambiguationData":[TD([[makeQuery(id+"F0.imprint","IMPRINT",EDGE,{"disambiguationData":[TD([[subQ8,-1.0]])],"derivedFrom":subQ6}),-1.0]])]});}
            var Q58;
            {var subQ0=sQuery(id+"F0.wireOp",EDGE,"E9");var subQ1=sQuery(id+"F0.wireOp",EDGE,"E2");var subQ2=makeQuery(id+"F0.imprint","INTERSECT",VERTEX,{"disambiguationData":[OD(1.0)],"derivedFrom":[subQ1,subQ0]});Q58=makeQuery(id+"F0.imprint","IMPRINT",FACE,{"disambiguationData":[TD([[makeQuery(id+"F0.imprint","IMPRINT",EDGE,{"disambiguationData":[TD([[subQ2,-1.0]])],"derivedFrom":subQ1}),-1.0]])]});}
            var Q59;
            {var subQ3=sQuery(id+"F0.wireOp",EDGE,"E9");var subQ5=sQuery(id+"F0.wireOp",EDGE,"E2");var subQ6=makeQuery(id+"F0.imprint","INTERSECT",VERTEX,{"disambiguationData":[OD(1.0)],"derivedFrom":[subQ5,subQ3]});Q59=makeQuery(id+"F0.imprint","IMPRINT",FACE,{"disambiguationData":[TD([[makeQuery(id+"F0.imprint","IMPRINT",EDGE,{"disambiguationData":[TD([[subQ6,-1.0]])],"derivedFrom":subQ5}),1.0]])]});}
            var Q60;
            {var subQ0=sQuery(id+"F0.wireOp",EDGE,"E13");var subQ1=sQuery(id+"F0.wireOp",EDGE,"E1");var subQ2=makeQuery(id+"F0.imprint","INTERSECT",VERTEX,{"disambiguationData":[OD(1.0)],"derivedFrom":[subQ1,subQ0]});Q60=makeQuery(id+"F0.imprint","IMPRINT",FACE,{"disambiguationData":[TD([[makeQuery(id+"F0.imprint","IMPRINT",EDGE,{"disambiguationData":[TD([[subQ2,-1.0]])],"derivedFrom":subQ1}),-1.0]])]});}
            var Q61;
            {var subQ0=sQuery(id+"F0.wireOp",EDGE,"E13");var subQ1=sQuery(id+"F0.wireOp",EDGE,"E1");var subQ2=makeQuery(id+"F0.imprint","INTERSECT",VERTEX,{"disambiguationData":[OD(1.0)],"derivedFrom":[subQ1,subQ0]});Q61=makeQuery(id+"F0.imprint","IMPRINT",FACE,{"disambiguationData":[TD([[makeQuery(id+"F0.imprint","IMPRINT",EDGE,{"disambiguationData":[TD([[subQ2,-1.0]])],"derivedFrom":subQ1}),1.0]])]});}
            var Q62;
            {var subQ0=sQuery(id+"F0.wireOp",EDGE,"E14");var subQ1=sQuery(id+"F0.wireOp",EDGE,"E2");var subQ2=makeQuery(id+"F0.imprint","INTERSECT",VERTEX,{"disambiguationData":[OD(0.0)],"derivedFrom":[subQ1,subQ0]});Q62=makeQuery(id+"F0.imprint","IMPRINT",FACE,{"disambiguationData":[TD([[makeQuery(id+"F0.imprint","IMPRINT",EDGE,{"disambiguationData":[TD([[subQ2,-1.0]])],"derivedFrom":subQ1}),-1.0]])]});}
            var Q63;
            {var subQ0=sQuery(id+"F0.wireOp",EDGE,"E15");var subQ1=sQuery(id+"F0.wireOp",EDGE,"E8");var subQ2=makeQuery(id+"F0.imprint","INTERSECT",VERTEX,{"derivedFrom":[subQ1,subQ0]});Q63=makeQuery(id+"F0.imprint","IMPRINT",FACE,{"disambiguationData":[TD([[makeQuery(id+"F0.imprint","IMPRINT",EDGE,{"disambiguationData":[TD([[subQ2,-1.0]])],"derivedFrom":subQ1}),-1.0]])]});}
            var Q64;
            {var subQ0=sQuery(id+"F0.wireOp",EDGE,"E15");var subQ1=sQuery(id+"F0.wireOp",EDGE,"E2");var subQ2=makeQuery(id+"F0.imprint","INTERSECT",VERTEX,{"derivedFrom":[subQ1,subQ0]});Q64=makeQuery(id+"F0.imprint","IMPRINT",FACE,{"disambiguationData":[TD([[makeQuery(id+"F0.imprint","IMPRINT",EDGE,{"disambiguationData":[TD([[subQ2,-1.0]])],"derivedFrom":subQ1}),-1.0]])]});}
            var Q65;
            {var subQ1=sQuery(id+"F0.wireOp",EDGE,"E2");var subQ7=sQuery(id+"F0.wireOp",EDGE,"E15");var subQ9=makeQuery(id+"F0.imprint","INTERSECT",VERTEX,{"derivedFrom":[subQ1,subQ7]});Q65=makeQuery(id+"F0.imprint","IMPRINT",FACE,{"disambiguationData":[TD([[makeQuery(id+"F0.imprint","IMPRINT",EDGE,{"disambiguationData":[TD([[subQ9,-1.0]])],"derivedFrom":subQ1}),1.0]])]});}
            var Q66;
            {var subQ0=sQuery(id+"F0.wireOp",EDGE,"E31.top");var subQ1=sQuery(id+"F0.wireOp",EDGE,"E1");var subQ2=makeQuery(id+"F0.imprint","INTERSECT",VERTEX,{"derivedFrom":[subQ1,subQ0]});Q66=makeQuery(id+"F0.imprint","IMPRINT",FACE,{"disambiguationData":[TD([[makeQuery(id+"F0.imprint","IMPRINT",EDGE,{"disambiguationData":[TD([[subQ2,-1.0]])],"derivedFrom":subQ1}),-1.0]])]});}
            var Q67;
            {var subQ4=sQuery(id+"F0.wireOp",EDGE,"E3");var subQ6=sQuery(id+"F0.wireOp",EDGE,"E1");var subQ7=makeQuery(id+"F0.imprint","INTERSECT",VERTEX,{"disambiguationData":[OD(1.0)],"derivedFrom":[subQ6,subQ4]});Q67=makeQuery(id+"F0.imprint","IMPRINT",FACE,{"disambiguationData":[TD([[makeQuery(id+"F0.imprint","IMPRINT",EDGE,{"disambiguationData":[TD([[subQ7,-1.0]])],"derivedFrom":subQ6}),-1.0]])]});}
            var Q68;
            {var subQ0=sQuery(id+"F0.wireOp",EDGE,"E31.right");var subQ3=sQuery(id+"F0.wireOp",EDGE,"E31.top");var subQ5=makeQuery(id+"F0.imprint","INTERSECT",VERTEX,{"derivedFrom":[subQ3,subQ0]});Q68=makeQuery(id+"F0.imprint","IMPRINT",FACE,{"disambiguationData":[TD([[makeQuery(id+"F0.imprint","IMPRINT",EDGE,{"disambiguationData":[TD([[subQ5,1.0]])],"derivedFrom":subQ3}),-1.0]])]});}
            var Q69;
            {var subQ0=sQuery(id+"F0.wireOp",EDGE,"E5");var subQ5=sQuery(id+"F0.wireOp",EDGE,"E15");var subQ6=makeQuery(id+"F0.imprint","INTERSECT",VERTEX,{"derivedFrom":[subQ0,subQ5]});Q69=makeQuery(id+"F0.imprint","IMPRINT",FACE,{"disambiguationData":[TD([[makeQuery(id+"F0.imprint","IMPRINT",EDGE,{"disambiguationData":[TD([[subQ6,-1.0]])],"derivedFrom":subQ5}),-1.0]])]});}
            var Q70;
            {var subQ0=sQuery(id+"F0.wireOp",EDGE,"E15");var subQ1=sQuery(id+"F0.wireOp",EDGE,"E5");var subQ2=makeQuery(id+"F0.imprint","INTERSECT",VERTEX,{"derivedFrom":[subQ1,subQ0]});Q70=makeQuery(id+"F0.imprint","IMPRINT",FACE,{"disambiguationData":[TD([[makeQuery(id+"F0.imprint","IMPRINT",EDGE,{"disambiguationData":[TD([[subQ2,-1.0]])],"derivedFrom":subQ1}),-1.0]])]});}
            extrude(context, id + "F1", {"entities" : qUnion([Q0, Q1, Q2, Q3, Q4, Q5, Q6, Q7, Q8, Q9, Q10, Q11, Q12, Q13, Q14, Q15, Q16, Q17, Q18, Q19, Q20, Q21, Q22, Q23, Q24, Q25, Q26, Q27, Q28, Q29, Q30, Q31, Q32, Q33, Q34, Q35, Q36, Q37, Q38, Q39, Q40, Q41, Q42, Q43, Q44, Q45, Q46, Q47, Q48, Q49, Q50, Q51, Q52, Q53, Q54, Q55, Q56, Q57, Q58, Q59, Q60, Q61, Q62, Q63, Q64, Q65, Q66, Q67, Q68, Q69, Q70]), "depth" : 38.1 * mm});
        }
        {
            var Q0;
            Q0=makeQuery(id+"F1.opExtrude","SWEPT_FACE",FACE,{"disambiguationData":[OSD([sQuery(id+"F0.wireOp",EDGE,"E31.right")])]});
            var sketch = newSketch(context, id + "F2", { "sketchPlane" : qUnion([Q0])});
            skLineSegment(sketch, "E39.bottom", {"start": v(0, 4.13) * mm, "end": v(38.1, 4.13) * mm});
            skLineSegment(sketch, "E39.top", {"start": v(0, -5.4) * mm, "end": v(38.1, -5.4) * mm});
            skLineSegment(sketch, "E39.left", {"start": v(0, 4.13) * mm, "end": v(0, -5.4) * mm});
            skLineSegment(sketch, "E39.right", {"start": v(38.1, 4.13) * mm, "end": v(38.1, -5.4) * mm});
            skLineSegment(sketch, "E40", {"start": v(-0.99, -0.64) * mm, "end": v(26.13, -0.64) * mm});
            skPoint(sketch, "E40.startSnap0", {"position": v(0, -0.64) * mm});
            skPoint(sketch, "E40.endSnap0", {"position": v(38.1, -0.64) * mm});
            skCircle(sketch, "E41", {"center": v(4.76, -0.64) * mm, "radius": 4.76 * mm});
            skLineSegment(sketch, "E42", {"start": v(4.76, -13.6) * mm, "end": v(4.76, 14.3) * mm});
            skLineSegment(sketch, "E43", {"start": v(4.76, -0.64) * mm, "end": v(7.4, 14.32) * mm});
            skLineSegment(sketch, "E44.bottom", {"start": v(4.76, 14.3) * mm, "end": v(-5.69, 14.3) * mm});
            skLineSegment(sketch, "E44.top", {"start": v(4.76, -13.6) * mm, "end": v(-5.69, -13.6) * mm});
            skLineSegment(sketch, "E44.left", {"start": v(4.76, 14.3) * mm, "end": v(4.76, -13.6) * mm});
            skLineSegment(sketch, "E44.right", {"start": v(-5.69, 14.3) * mm, "end": v(-5.69, -13.6) * mm});
            skLineSegment(sketch, "E45", {"start": v(4.76, -0.64) * mm, "end": v(20.91, -14.19) * mm});
            skLineSegment(sketch, "E46", {"start": v(20.91, -14.19) * mm, "end": v(4.76, -14.19) * mm});
            skLineSegment(sketch, "E47", {"start": v(4.76, -14.19) * mm, "end": v(4.76, -13.6) * mm});
            skLineSegment(sketch, "E48", {"start": v(4.76, 14.3) * mm, "end": v(7.4, 14.32) * mm});
            skSolve(sketch);
        }
        {
            var Q0;
            {var subQ0=sQuery(id+"F2.wireOp",EDGE,"E46");Q0=makeQuery(id+"F2.imprint","IMPRINT",FACE,{"disambiguationData":[TD([[makeQuery(id+"F2.imprint","IMPRINT",EDGE,{"derivedFrom":subQ0}),-1.0]])]});}
            var Q1;
            {var subQ11=sQuery(id+"F2.wireOp",EDGE,"E44.bottom");Q1=makeQuery(id+"F2.imprint","IMPRINT",FACE,{"disambiguationData":[TD([[makeQuery(id+"F2.imprint","IMPRINT",EDGE,{"derivedFrom":subQ11}),1.0]])]});}
            var Q2;
            {var subQ5=sQuery(id+"F2.wireOp",EDGE,"E48");Q2=makeQuery(id+"F2.imprint","IMPRINT",FACE,{"disambiguationData":[TD([[makeQuery(id+"F2.imprint","IMPRINT",EDGE,{"derivedFrom":subQ5}),-1.0]])]});}
            var Q3;
            {var subQ0=sQuery(id+"F2.wireOp",EDGE,"E39.left");var subQ1=sQuery(id+"F2.wireOp",EDGE,"E39.bottom");var subQ2=makeQuery(id+"F2.imprint","INTERSECT",VERTEX,{"derivedFrom":[subQ1,subQ0]});Q3=makeQuery(id+"F2.imprint","IMPRINT",FACE,{"disambiguationData":[TD([[makeQuery(id+"F2.imprint","IMPRINT",EDGE,{"disambiguationData":[TD([[subQ2,1.0]])],"derivedFrom":subQ1}),1.0]])]});}
            var Q4;
            {var subQ0=sQuery(id+"F2.wireOp",EDGE,"E39.left");var subQ1=sQuery(id+"F2.wireOp",EDGE,"E39.top");var subQ2=makeQuery(id+"F2.imprint","INTERSECT",VERTEX,{"derivedFrom":[subQ1,subQ0]});Q4=makeQuery(id+"F2.imprint","IMPRINT",FACE,{"disambiguationData":[TD([[makeQuery(id+"F2.imprint","IMPRINT",EDGE,{"disambiguationData":[TD([[subQ2,1.0]])],"derivedFrom":subQ1}),-1.0]])]});}
            extrude(context, id + "F3", {"entities" : qUnion([Q0, Q1, Q2, Q3, Q4]), "operationType" : NewBodyOperationType.REMOVE, "oppositeDirection" : true, "depth" : 25.4 * mm});
        }
        {
            var Q0;
            Q0=makeQuery(id+"F3.boolean.opBoolean","MERGE",FACE,{"derivedFrom":[makeQuery(id+"F1.opExtrude","SWEPT_FACE",FACE,{"disambiguationData":[OSD([sQuery(id+"F0.wireOp",EDGE,"E31.top")])]}),makeQuery(id+"F3.opExtrude","SWEPT_FACE",FACE,{"disambiguationData":[OSD([sQuery(id+"F2.wireOp",EDGE,"E39.top")])]})]});
            var sketch = newSketch(context, id + "F4", { "sketchPlane" : qUnion([Q0])});
            skLineSegment(sketch, "E49.bottom", {"start": v(-12.25, 10.44) * mm, "end": v(-9.53, 10.44) * mm});
            skLineSegment(sketch, "E49.top", {"start": v(-12.25, -2.19) * mm, "end": v(-9.53, -2.19) * mm});
            skLineSegment(sketch, "E49.left", {"start": v(-12.25, 10.44) * mm, "end": v(-12.25, -2.19) * mm});
            skLineSegment(sketch, "E49.right", {"start": v(-9.53, 10.44) * mm, "end": v(-9.53, -2.19) * mm});
            skLineSegment(sketch, "E50.bottom", {"start": v(-12.25, 10.44) * mm, "end": v(-11.12, 10.44) * mm});
            skLineSegment(sketch, "E50.top", {"start": v(-12.25, 0) * mm, "end": v(-11.12, 0) * mm});
            skLineSegment(sketch, "E50.left", {"start": v(-12.25, 10.44) * mm, "end": v(-12.25, 0) * mm});
            skLineSegment(sketch, "E50.right", {"start": v(-11.12, 10.44) * mm, "end": v(-11.12, 0) * mm});
            skSolve(sketch);
        }
        {
            var Q0;
            {var subQ2=sQuery(id+"F4.wireOp",EDGE,"E49.top");Q0=makeQuery(id+"F4.imprint","IMPRINT",FACE,{"disambiguationData":[TD([[makeQuery(id+"F4.imprint","IMPRINT",EDGE,{"derivedFrom":subQ2}),1.0]])]});}
            var Q1;
            {var subQ1=sQuery(id+"F2.wireOp",EDGE,"E39.top");var subQ4=sQuery(id+"F4.wireOp",EDGE,"E49.bottom");var subQ8=sQuery(id+"F4.wireOp",EDGE,"E49.right");var subQ9=makeQuery(id+"F4.imprint","INTERSECT",VERTEX,{"derivedFrom":[makeQuery(id+"F3.boolean.opBoolean","COPY",EDGE,{"derivedFrom":makeQuery(id+"F3.opExtrude","SWEPT_EDGE",EDGE,{"disambiguationData":[OSD([subQ1,sQuery(id+"F2.wireOp",EDGE,"E45")])]})}),subQ4,subQ8]});Q1=makeQuery(id+"F4.imprint","IMPRINT",FACE,{"disambiguationData":[TD([[makeQuery(id+"F4.imprint","IMPRINT",EDGE,{"disambiguationData":[TD([[subQ9,-1.0]])],"derivedFrom":subQ4}),1.0]])]});}
            var Q2;
            {var subQ3=sQuery(id+"F4.wireOp",EDGE,"E50.bottom");Q2=makeQuery(id+"F4.imprint","IMPRINT",FACE,{"disambiguationData":[TD([[makeQuery(id+"F4.imprint","IMPRINT",EDGE,{"derivedFrom":subQ3}),-1.0]])]});}
            var Q3;
            Q3=makeQuery(id+"F3.boolean.opBoolean","MERGE",FACE,{"derivedFrom":[makeQuery(id+"F1.opExtrude","SWEPT_FACE",FACE,{"disambiguationData":[OSD([sQuery(id+"F0.wireOp",EDGE,"E31.bottom")])]}),makeQuery(id+"F3.opExtrude","SWEPT_FACE",FACE,{"disambiguationData":[OSD([sQuery(id+"F2.wireOp",EDGE,"E39.bottom")])]})]});
            extrude(context, id + "F5", {"entities" : qUnion([Q0, Q1, Q2]), "operationType" : NewBodyOperationType.REMOVE, "endBound" : BoundingType.UP_TO_SURFACE, "oppositeDirection" : true, "endBoundEntityFace" : qUnion([Q3]), "depth" : 25.4 * mm});
        }
        {
            var Q0;
            Q0=makeQuery(id+"F5.boolean.opBoolean","COPY",FACE,{"derivedFrom":makeQuery(id+"F5.opExtrude","SWEPT_FACE",FACE,{"disambiguationData":[OSD([sQuery(id+"F4.wireOp",EDGE,"E49.right")])]})});
            var sketch = newSketch(context, id + "F6", { "sketchPlane" : qUnion([Q0])});
            skCircle(sketch, "E51", {"center": v(4.76, -0.64) * mm, "radius": 4.76 * mm});
            skCircle(sketch, "E52", {"center": v(4.76, -0.64) * mm, "radius": 2.38 * mm});
            skSolve(sketch);
        }
        {
            var Q0;
            Q0=makeQuery(id+"F6.imprint","IMPRINT",FACE,{"disambiguationData":[TD([[makeQuery(id+"F6.imprint","IMPRINT",EDGE,{"derivedFrom":sQuery(id+"F6.wireOp",EDGE,"E52")}),1.0]])]});
            extrude(context, id + "F7", {"entities" : qUnion([Q0]), "operationType" : NewBodyOperationType.REMOVE, "oppositeDirection" : true, "depth" : 25.4 * mm});
        }
        {
            var Q0;
            Q0=makeQuery(id+"F1.opExtrude","SWEPT_FACE",FACE,{"disambiguationData":[OSD([sQuery(id+"F0.wireOp",EDGE,"E36.top"),sQuery(id+"F0.wireOp",EDGE,"E37.top")])]});
            var sketch = newSketch(context, id + "F8", { "sketchPlane" : qUnion([Q0])});
            skCircle(sketch, "E53", {"center": v(-0.02, 24.36) * mm, "radius": 6.35 * mm});
            skPoint(sketch, "E53.centerSnap0", {"position": v(-0.02, 18) * mm});
            skLineSegment(sketch, "E54.bottom", {"start": v(12.28, 24.36) * mm, "end": v(-16.78, 24.36) * mm});
            skLineSegment(sketch, "E54.top", {"start": v(12.28, 41.87) * mm, "end": v(-16.78, 41.87) * mm});
            skLineSegment(sketch, "E54.left", {"start": v(12.28, 24.36) * mm, "end": v(12.28, 41.87) * mm});
            skLineSegment(sketch, "E54.right", {"start": v(-16.78, 24.36) * mm, "end": v(-16.78, 41.87) * mm});
            skLineSegment(sketch, "E55", {"start": v(-0.02, 14.92) * mm, "end": v(-0.02, 46.19) * mm});
            skSolve(sketch);
        }
        {
            var Q0;
            {var subQ0=sQuery(id+"F8.wireOp",EDGE,"E55");var subQ1=sQuery(id+"F8.wireOp",EDGE,"E53");var subQ2=makeQuery(id+"F8.imprint","INTERSECT",VERTEX,{"derivedFrom":[subQ1,subQ0]});Q0=makeQuery(id+"F8.imprint","IMPRINT",FACE,{"disambiguationData":[TD([[makeQuery(id+"F8.imprint","IMPRINT",EDGE,{"disambiguationData":[TD([[subQ2,1.0]])],"derivedFrom":subQ1}),-1.0]])]});}
            var Q1;
            {var subQ0=sQuery(id+"F8.wireOp",EDGE,"E54.left");Q1=makeQuery(id+"F8.imprint","IMPRINT",FACE,{"disambiguationData":[TD([[makeQuery(id+"F8.imprint","IMPRINT",EDGE,{"derivedFrom":subQ0}),1.0]])]});}
            var Q2;
            {var subQ0=sQuery(id+"F8.wireOp",EDGE,"E55");var subQ1=sQuery(id+"F8.wireOp",EDGE,"E53");var subQ2=makeQuery(id+"F8.imprint","INTERSECT",VERTEX,{"derivedFrom":[subQ1,subQ0]});Q2=makeQuery(id+"F8.imprint","IMPRINT",FACE,{"disambiguationData":[TD([[makeQuery(id+"F8.imprint","IMPRINT",EDGE,{"disambiguationData":[TD([[subQ2,-1.0]])],"derivedFrom":subQ1}),-1.0]])]});}
            var Q3;
            {var subQ0=sQuery(id+"F8.wireOp",EDGE,"E54.right");Q3=makeQuery(id+"F8.imprint","IMPRINT",FACE,{"disambiguationData":[TD([[makeQuery(id+"F8.imprint","IMPRINT",EDGE,{"derivedFrom":subQ0}),-1.0]])]});}
            extrude(context, id + "F9", {"entities" : qUnion([Q0, Q1, Q2, Q3]), "operationType" : NewBodyOperationType.REMOVE, "oppositeDirection" : true, "depth" : 25.4 * mm});
        }
        {
            var Q0;
            {var subQ0=sQuery(id+"F8.wireOp",EDGE,"E54.bottom");Q0=makeQuery(id+"F9.boolean.opBoolean","COPY",FACE,{"derivedFrom":makeQuery(id+"F9.opExtrude","SWEPT_FACE",FACE,{"disambiguationData":[OSD([subQ0]),TDD([makeQuery(id+"F8.imprint","IMPRINT",EDGE,{"disambiguationData":[TD([[makeQuery(id+"F8.imprint","INTERSECT",VERTEX,{"derivedFrom":[subQ0,sQuery(id+"F8.wireOp",EDGE,"E54.right")]}),1.0]])],"derivedFrom":subQ0})])]})});}
            var sketch = newSketch(context, id + "F10", { "sketchPlane" : qUnion([Q0])});
            skLineSegment(sketch, "E56.bottom", {"start": v(-6.37, 10.54) * mm, "end": v(6.33, 10.54) * mm});
            skLineSegment(sketch, "E56.top", {"start": v(-6.37, -11.68) * mm, "end": v(6.33, -11.68) * mm});
            skLineSegment(sketch, "E56.left", {"start": v(-6.37, 10.54) * mm, "end": v(-6.37, -11.68) * mm});
            skLineSegment(sketch, "E56.right", {"start": v(6.33, 10.54) * mm, "end": v(6.33, -11.68) * mm});
            skLineSegment(sketch, "E57.bottom", {"start": v(-6.37, 0) * mm, "end": v(6.33, 0) * mm});
            skLineSegment(sketch, "E57.top", {"start": v(-6.37, 7.37) * mm, "end": v(6.33, 7.37) * mm});
            skLineSegment(sketch, "E57.left", {"start": v(-6.37, 0) * mm, "end": v(-6.37, 7.37) * mm});
            skLineSegment(sketch, "E57.right", {"start": v(6.33, 0) * mm, "end": v(6.33, 7.37) * mm});
            skLineSegment(sketch, "E58.top", {"start": v(-6.37, -8.5) * mm, "end": v(6.33, -8.5) * mm});
            skLineSegment(sketch, "E58.left", {"start": v(-6.37, 0) * mm, "end": v(-6.37, -8.5) * mm});
            skLineSegment(sketch, "E58.right", {"start": v(6.33, 0) * mm, "end": v(6.33, -8.5) * mm});
            skSolve(sketch);
        }
        {
            var Q0;
            {var subQ4=sQuery(id+"F10.wireOp",EDGE,"E57.top");Q0=makeQuery(id+"F10.imprint","IMPRINT",FACE,{"disambiguationData":[TD([[makeQuery(id+"F10.imprint","IMPRINT",EDGE,{"derivedFrom":subQ4}),-1.0]])]});}
            var Q1;
            {var subQ4=sQuery(id+"F10.wireOp",EDGE,"E57.bottom");Q1=makeQuery(id+"F10.imprint","IMPRINT",FACE,{"disambiguationData":[TD([[makeQuery(id+"F10.imprint","IMPRINT",EDGE,{"derivedFrom":subQ4}),-1.0]])]});}
            extrude(context, id + "F11", {"entities" : qUnion([Q0, Q1]), "operationType" : NewBodyOperationType.REMOVE, "depth" : 25.4 * mm});
        }
        {
            var Q0;
            Q0=makeQuery(id+"F1.opExtrude","SWEPT_FACE",FACE,{"disambiguationData":[OSD([sQuery(id+"F0.wireOp",EDGE,"E33.top")])]});
            var sketch = newSketch(context, id + "F12", { "sketchPlane" : qUnion([Q0])});
            skCircle(sketch, "E59", {"center": v(-0.02, -24.36) * mm, "radius": 3.18 * mm});
            skSolve(sketch);
        }
        {
            var Q0;
            Q0 = qSketchRegion(id + "F12", true);
            extrude(context, id + "F13", {"entities" : qUnion([Q0]), "operationType" : NewBodyOperationType.REMOVE, "oppositeDirection" : true, "depth" : 25.4 * mm});
        }
    });
